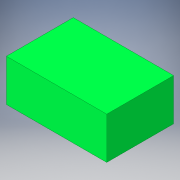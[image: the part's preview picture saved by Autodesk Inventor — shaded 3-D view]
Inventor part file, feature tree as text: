
AUTODESK INVENTOR PART (.ipt)
format: ipt  version: 2016 (Build 200138000, 138)  size: 91,648 bytes
history: native  units: in
note: dims shown in document units (in); Inventor stores cm internally (conversion verified against a paired STEP export)
features: extrude x1, sketch x1
ambient origin geometry x8: Origin, YZ Plane, XZ Plane, XY Plane, X Axis, Y Axis, Z Axis, Center Point
bodies: Solid1 (feature_tree)
feature tree (2):
  extrude  "Extrusion1"  Depth=1.25in
  sketch  "Sketch1"  dims[d0=3.0in d1=1.25in d2=2.0in d3=0.0in]
